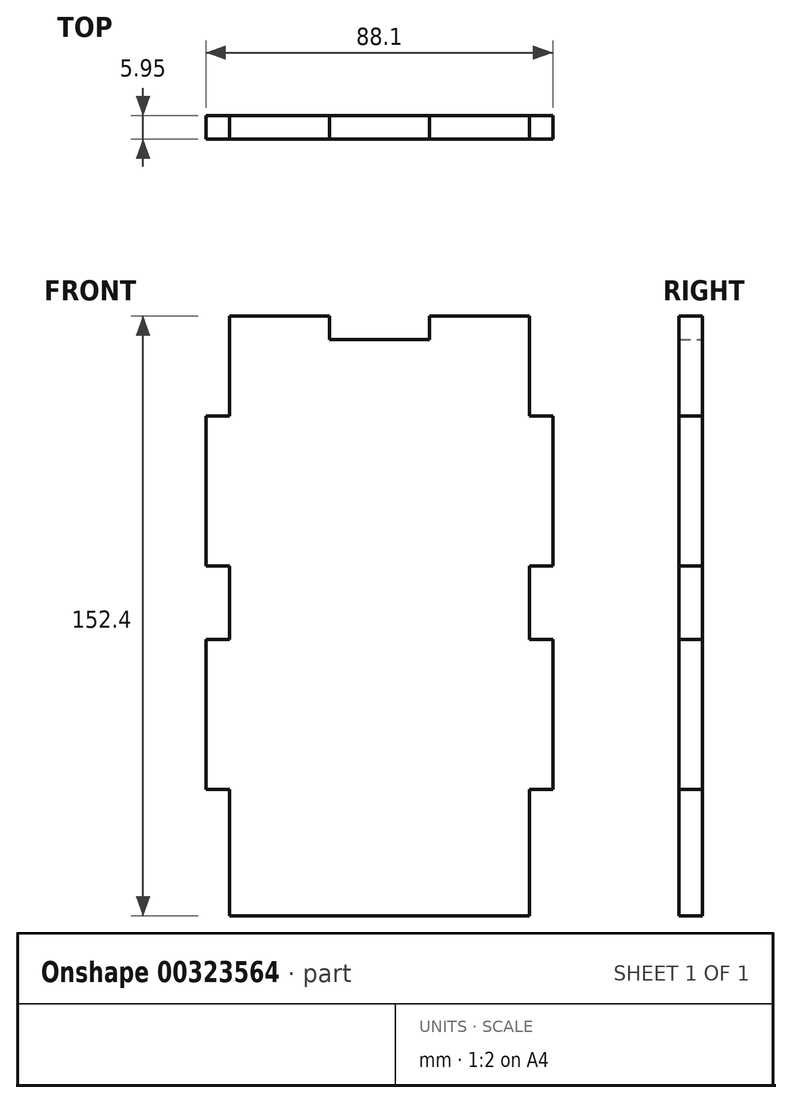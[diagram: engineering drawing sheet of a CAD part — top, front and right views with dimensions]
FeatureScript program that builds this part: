
annotation { "Feature Type Name" : "Feature", "Feature Type Description" : "" }
export const myFeature = defineFeature(function(context is Context, id is Id, definition is map)
    precondition{}
    {
        {
            var Q0;
            Q0=qCreatedBy(makeId("Front.planeOp"),FACE);
            var sketch = newSketch(context, id + "F0", { "sketchPlane" : qUnion([Q0])});
            skLineSegment(sketch, "E0.bottom", {"start": v(-46.4, 66.27) * mm, "end": v(29.8, 66.27) * mm});
            skLineSegment(sketch, "E0.top", {"start": v(-46.4, -86.13) * mm, "end": v(29.8, -86.13) * mm});
            skLineSegment(sketch, "E0.left", {"start": v(-46.4, 66.27) * mm, "end": v(-46.4, -86.13) * mm});
            skLineSegment(sketch, "E0.right", {"start": v(29.8, 66.27) * mm, "end": v(29.8, -86.13) * mm});
            skLineSegment(sketch, "E1.bottom", {"start": v(-21, 66.27) * mm, "end": v(4.4, 66.27) * mm});
            skLineSegment(sketch, "E1.top", {"start": v(-21, 60.32) * mm, "end": v(4.4, 60.32) * mm});
            skLineSegment(sketch, "E1.left", {"start": v(-21, 66.27) * mm, "end": v(-21, 60.32) * mm});
            skLineSegment(sketch, "E1.right", {"start": v(4.4, 66.27) * mm, "end": v(4.4, 60.32) * mm});
            skLineSegment(sketch, "E2.bottom", {"start": v(29.8, 40.87) * mm, "end": v(35.74, 40.87) * mm});
            skLineSegment(sketch, "E2.top", {"start": v(29.8, 2.77) * mm, "end": v(35.74, 2.77) * mm});
            skLineSegment(sketch, "E2.left", {"start": v(29.8, 40.87) * mm, "end": v(29.8, 2.77) * mm});
            skLineSegment(sketch, "E2.right", {"start": v(35.74, 40.87) * mm, "end": v(35.74, 2.77) * mm});
            skLineSegment(sketch, "E3.bottom", {"start": v(29.8, -53.98) * mm, "end": v(35.74, -53.98) * mm});
            skLineSegment(sketch, "E3.top", {"start": v(29.8, -15.88) * mm, "end": v(35.74, -15.88) * mm});
            skLineSegment(sketch, "E3.left", {"start": v(29.8, -53.98) * mm, "end": v(29.8, -15.88) * mm});
            skLineSegment(sketch, "E3.right", {"start": v(35.74, -53.98) * mm, "end": v(35.74, -15.88) * mm});
            skLineSegment(sketch, "E4.bottom", {"start": v(-46.4, -53.98) * mm, "end": v(-52.36, -53.98) * mm});
            skLineSegment(sketch, "E4.top", {"start": v(-46.4, -15.88) * mm, "end": v(-52.36, -15.88) * mm});
            skLineSegment(sketch, "E4.left", {"start": v(-46.4, -53.98) * mm, "end": v(-46.4, -15.88) * mm});
            skLineSegment(sketch, "E4.right", {"start": v(-52.36, -53.98) * mm, "end": v(-52.36, -15.88) * mm});
            skLineSegment(sketch, "E5.bottom", {"start": v(-46.4, 2.77) * mm, "end": v(-52.36, 2.77) * mm});
            skLineSegment(sketch, "E5.top", {"start": v(-46.4, 40.87) * mm, "end": v(-52.36, 40.87) * mm});
            skLineSegment(sketch, "E5.left", {"start": v(-46.4, 2.77) * mm, "end": v(-46.4, 40.87) * mm});
            skLineSegment(sketch, "E5.right", {"start": v(-52.36, 2.77) * mm, "end": v(-52.36, 40.87) * mm});
            skSolve(sketch);
        }
        {
            var Q0;
            {var subQ1=sQuery(id+"F0.wireOp",EDGE,"E0.top");Q0=makeQuery(id+"F0.imprint","IMPRINT",FACE,{"disambiguationData":[TD([[makeQuery(id+"F0.imprint","IMPRINT",EDGE,{"derivedFrom":subQ1}),1.0]])]});}
            var Q1;
            Q1=makeQuery(id+"F0.imprint","IMPRINT",FACE,{"disambiguationData":[TD([[makeQuery(id+"F0.imprint","IMPRINT",EDGE,{"derivedFrom":sQuery(id+"F0.wireOp",EDGE,"E5.bottom")}),-1.0]])]});
            var Q2;
            Q2=makeQuery(id+"F0.imprint","IMPRINT",FACE,{"disambiguationData":[TD([[makeQuery(id+"F0.imprint","IMPRINT",EDGE,{"derivedFrom":sQuery(id+"F0.wireOp",EDGE,"E4.bottom")}),-1.0]])]});
            var Q3;
            Q3=makeQuery(id+"F0.imprint","IMPRINT",FACE,{"disambiguationData":[TD([[makeQuery(id+"F0.imprint","IMPRINT",EDGE,{"derivedFrom":sQuery(id+"F0.wireOp",EDGE,"E3.bottom")}),1.0]])]});
            var Q4;
            Q4=makeQuery(id+"F0.imprint","IMPRINT",FACE,{"disambiguationData":[TD([[makeQuery(id+"F0.imprint","IMPRINT",EDGE,{"derivedFrom":sQuery(id+"F0.wireOp",EDGE,"E2.bottom")}),-1.0]])]});
            extrude(context, id + "F1", {"entities" : qUnion([Q0, Q1, Q2, Q3, Q4]), "depth" : 5.95 * mm});
        }
    });
